FCSTD DOCUMENT  (FreeCAD 1.0R38642 (Git))
Label: rounded_rect_with_center_circle
License: All rights reserved
LicenseURL: http://en.wikipedia.org/wiki/All_rights_reserved
objects: Sketcher::SketchObject×1
note: 2 computed .brp shape members not serialized (recipe doc carries the construction recipe); baked Part::Feature solids carry a one-line shape summary decoded from their .brp

FEATURE [Sketcher::SketchObject] Sketch006  label="xz_rounded_rectangle_with_circle"
  ArcFitTolerance = 1e-06
  FullyConstrained = true
  MakeInternals = false
  Placement = pos=(0,0,0) rot=(1,0,0;1.5708rad)
  sketch-geometry (11):
    g0: LineSegment StartX=19.05 StartY=25.4 StartZ=0 EndX=57.15 EndY=25.4 EndZ=0
    g1: LineSegment StartX=63.5 StartY=31.75 StartZ=0 EndX=63.5 EndY=44.45 EndZ=0
    g2: LineSegment StartX=57.15 StartY=50.8 StartZ=0 EndX=19.05 EndY=50.8 EndZ=0
    g3: LineSegment StartX=12.7 StartY=44.45 StartZ=0 EndX=12.7 EndY=31.75 EndZ=0
    g4: ArcOfCircle CenterX=19.05 CenterY=31.75 CenterZ=0 NormalX=0 NormalY=0 NormalZ=1 AngleXU=0 Radius=6.35 StartAngle=3.14159 EndAngle=4.71239
    g5: ArcOfCircle CenterX=57.15 CenterY=31.75 CenterZ=0 NormalX=0 NormalY=0 NormalZ=1 AngleXU=0 Radius=6.35 StartAngle=4.71239 EndAngle=6.28319
    g6: ArcOfCircle CenterX=57.15 CenterY=44.45 CenterZ=0 NormalX=0 NormalY=0 NormalZ=1 AngleXU=0 Radius=6.35 StartAngle=0 EndAngle=1.5708
    g7: ArcOfCircle CenterX=19.05 CenterY=44.45 CenterZ=0 NormalX=0 NormalY=0 NormalZ=1 AngleXU=0 Radius=6.35 StartAngle=1.5708 EndAngle=3.14159
    g8: GeomPoint [constr] X=12.7 Y=25.4 Z=0
    g9: GeomPoint [constr] X=63.5 Y=50.8 Z=0
    g10: Circle CenterX=38.1 CenterY=38.1 CenterZ=0 NormalX=0 NormalY=0 NormalZ=1 AngleXU=0 Radius=6.35
  constraints (27):
    c: Tangent(g0,g4) = -1.5708
    c: Tangent(g0,g5) = -1.5708
    c: Tangent(g1,g5) = -1.5708
    c: Tangent(g1,g6) = -1.5708
    c: Tangent(g2,g6) = -1.5708
    c: Tangent(g2,g7) = -1.5708
    c: Tangent(g3,g7) = -1.5708
    c: Tangent(g3,g4) = -1.5708
    c: Horizontal(g0)
    c: Horizontal(g2)
    c: Vertical(g1)
    c: Vertical(g3)
    c: Equal(g4,g5)
    c: Equal(g5,g6)
    c: Equal(g6,g7)
    c: PointOnObject(g8,g0)
    c: PointOnObject(g8,g3)
    c: PointOnObject(g9,g1)
    c: PointOnObject(g9,g2)
    c: Radius(g7) = 6.35
    c: Distance(g0,g2) = 25.4
    c: Distance(g1,g3) = 50.8
    c: Distance(g-1,g0) = 25.4
    c: Distance(g-2,g3) = 12.7
    c: Distance(g10,g3) = 25.4
    c: Distance(g10,g0) = 12.7
    c: Diameter(g10) = 12.7
